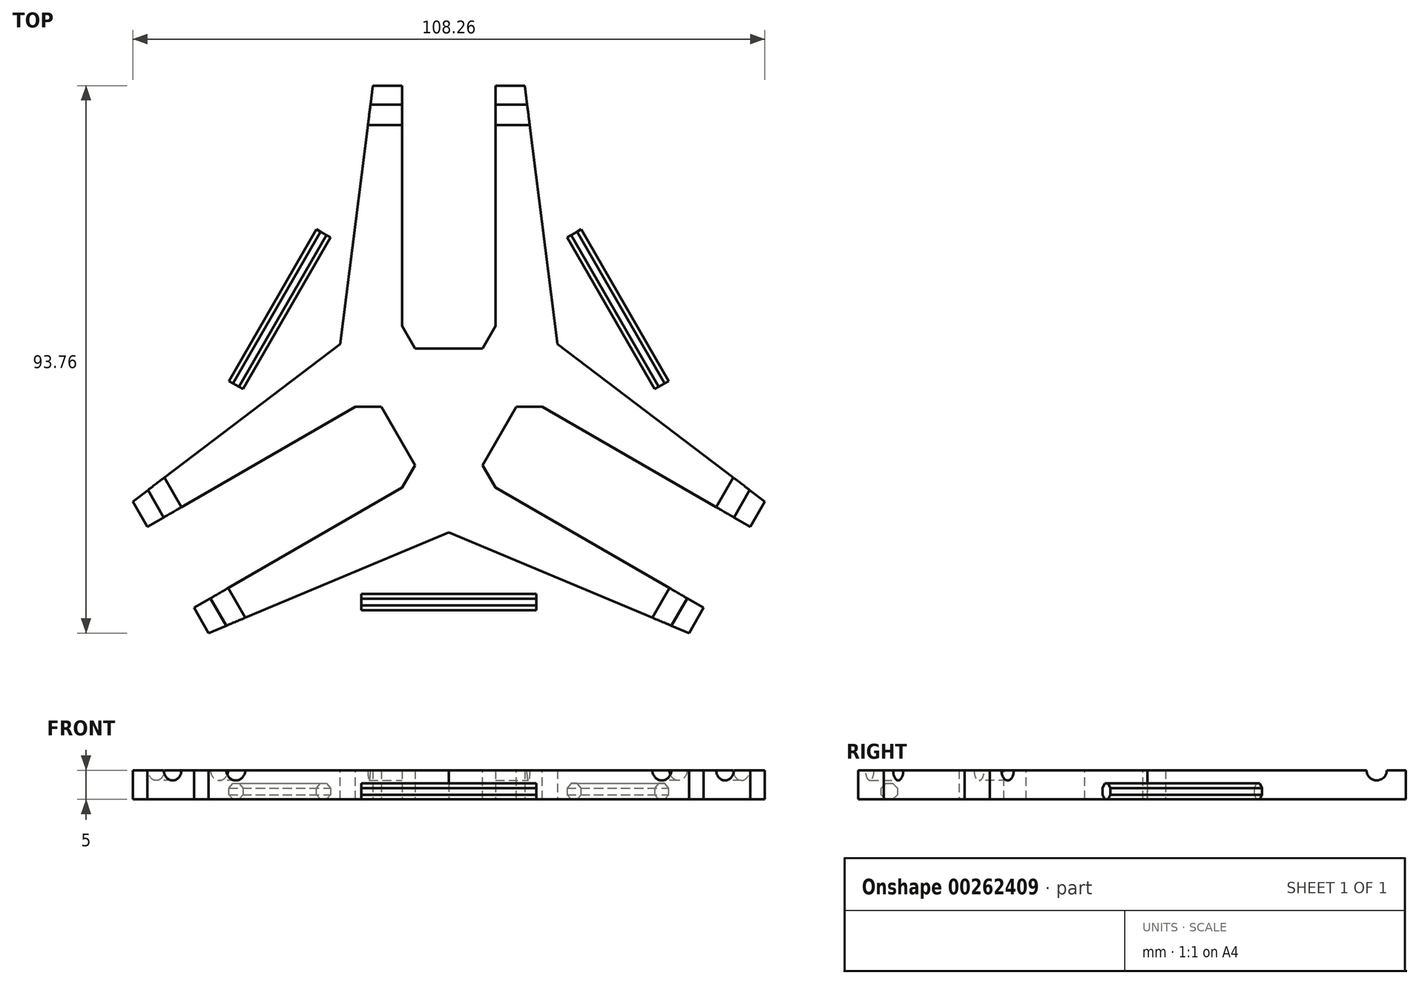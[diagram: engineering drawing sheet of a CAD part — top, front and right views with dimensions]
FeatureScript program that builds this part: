
annotation { "Feature Type Name" : "Feature", "Feature Type Description" : "" }
export const myFeature = defineFeature(function(context is Context, id is Id, definition is map)
    precondition{}
    {
        {
            var Q0;
            Q0=qCreatedBy(makeId("Top.planeOp"),FACE);
            var sketch = newSketch(context, id + "F0", { "sketchPlane" : qUnion([Q0])});
            skLineSegment(sketch, "E0", {"start": v(0, 0) * mm, "end": v(0, 10) * mm});
            skLineSegment(sketch, "E1", {"start": v(0, 10) * mm, "end": v(-8, 10) * mm});
            skLineSegment(sketch, "E2", {"start": v(-8, 10) * mm, "end": v(-8, 55) * mm});
            skLineSegment(sketch, "E3", {"start": v(-8, 55) * mm, "end": v(-13, 55) * mm});
            skLineSegment(sketch, "E4", {"start": v(-13, 55) * mm, "end": v(-20, 0) * mm});
            skLineSegment(sketch, "E5", {"start": v(-20, 0) * mm, "end": v(0, 0) * mm});
            skLineSegment(sketch, "E6.MirrorCS", {"start": v(0, 10) * mm, "end": v(8, 10) * mm});
            skLineSegment(sketch, "E7.MirrorCS", {"start": v(8, 10) * mm, "end": v(8, 55) * mm});
            skLineSegment(sketch, "E8.MirrorCS", {"start": v(8, 55) * mm, "end": v(13, 55) * mm});
            skLineSegment(sketch, "E9.MirrorCS", {"start": v(13, 55) * mm, "end": v(20, 0) * mm});
            skLineSegment(sketch, "E10.MirrorCS", {"start": v(20, 0) * mm, "end": v(0, 0) * mm});
            skSolve(sketch);
        }
        {
            var Q0;
            Q0=makeQuery(id+"F0.imprint","IMPRINT",FACE,{"disambiguationData":[TD([[makeQuery(id+"F0.imprint","IMPRINT",EDGE,{"derivedFrom":sQuery(id+"F0.wireOp",EDGE,"E0")}),-1.0]])]});
            var Q1;
            Q1=makeQuery(id+"F0.imprint","IMPRINT",FACE,{"disambiguationData":[TD([[makeQuery(id+"F0.imprint","IMPRINT",EDGE,{"derivedFrom":sQuery(id+"F0.wireOp",EDGE,"E0")}),1.0]])]});
            extrude(context, id + "F1", {"entities" : qUnion([Q0, Q1]), "depth" : 5 * mm});
        }
        {
            var Q0;
            Q0=qCreatedBy(makeId("Right.planeOp"),FACE);
            var sketch = newSketch(context, id + "F2", { "sketchPlane" : qUnion([Q0])});
            skLineSegment(sketch, "E11.0.0", {"start": v(0, 0) * mm, "end": v(55, 0) * mm, "construction": true});
            skLineSegment(sketch, "E11.0.1", {"start": v(55, 0) * mm, "end": v(55, 5) * mm, "construction": true});
            skLineSegment(sketch, "E11.0.2", {"start": v(55, 5) * mm, "end": v(0, 5) * mm, "construction": true});
            skLineSegment(sketch, "E11.0.3", {"start": v(0, 5) * mm, "end": v(0, 0) * mm, "construction": true});
            skCircle(sketch, "E12", {"center": v(50, 5) * mm, "radius": 1.75 * mm});
            skLineSegment(sketch, "E13", {"start": v(0, 24.2) * mm, "end": v(0, -16.8) * mm, "construction": true});
            skCircle(sketch, "E14.cCircle", {"center": v(-71.43, 1.39) * mm, "radius": 1.5 * mm, "construction": true});
            skLineSegment(sketch, "E14.0", {"start": v(-72, 0) * mm, "end": v(-72.82, 0.81) * mm});
            skLineSegment(sketch, "E14.1", {"start": v(-72.82, 0.81) * mm, "end": v(-72.82, 1.96) * mm});
            skLineSegment(sketch, "E14.2", {"start": v(-72.82, 1.96) * mm, "end": v(-72, 2.77) * mm});
            skLineSegment(sketch, "E14.3", {"start": v(-72, 2.77) * mm, "end": v(-70.86, 2.77) * mm});
            skLineSegment(sketch, "E14.4", {"start": v(-70.86, 2.77) * mm, "end": v(-70.05, 1.96) * mm});
            skLineSegment(sketch, "E14.5", {"start": v(-70.05, 1.96) * mm, "end": v(-70.05, 0.81) * mm});
            skLineSegment(sketch, "E14.6", {"start": v(-70.05, 0.81) * mm, "end": v(-70.86, 0) * mm});
            skLineSegment(sketch, "E14.7", {"start": v(-70.86, 0) * mm, "end": v(-72, 0) * mm});
            skSolve(sketch);
        }
        {
            var Q0;
            Q0=makeQuery(id+"F2.imprint","IMPRINT",FACE,{"disambiguationData":[TD([[makeQuery(id+"F2.imprint","IMPRINT",EDGE,{"derivedFrom":sQuery(id+"F2.wireOp",EDGE,"E12")}),1.0]])]});
            extrude(context, id + "F3", {"entities" : qUnion([Q0]), "operationType" : NewBodyOperationType.REMOVE, "endBound" : BoundingType.SYMMETRIC, "oppositeDirection" : true, "depth" : 50 * mm});
        }
        {
            var Q0;
            Q0=makeQuery(id+"F1.opExtrude","SWEPT_BODY",BODY,{"disambiguationData":[OSD([sQuery(id+"F0.wireOp",EDGE,"E1"),sQuery(id+"F0.wireOp",EDGE,"E2"),sQuery(id+"F0.wireOp",EDGE,"E3"),sQuery(id+"F0.wireOp",EDGE,"E4"),sQuery(id+"F0.wireOp",EDGE,"E5"),sQuery(id+"F0.wireOp",EDGE,"E6.MirrorCS"),sQuery(id+"F0.wireOp",EDGE,"E7.MirrorCS"),sQuery(id+"F0.wireOp",EDGE,"E8.MirrorCS"),sQuery(id+"F0.wireOp",EDGE,"E9.MirrorCS"),sQuery(id+"F0.wireOp",EDGE,"E10.MirrorCS")])]});
            var Q1;
            Q1=sQuery(id+"F2.wireOp",EDGE,"E13");
            circularPattern(context, id + "F4", {"operationType" : NewBodyOperationType.ADD, "entities" : qUnion([Q0]), "axis" : qUnion([Q1]), "angle" : 360 * degree, "instanceCount" : 3, "equalSpace" : true});
        }
        {
            var Q0;
            Q0=makeQuery(id+"F2.imprint","IMPRINT",FACE,{"disambiguationData":[TD([[makeQuery(id+"F2.imprint","IMPRINT",EDGE,{"derivedFrom":sQuery(id+"F2.wireOp",EDGE,"E14.0")}),-1.0]])]});
            extrude(context, id + "F5", {"entities" : qUnion([Q0]), "endBound" : BoundingType.SYMMETRIC, "depth" : 30 * mm});
        }
        {
            var Q0;
            Q0=makeQuery(id+"F5.opExtrude","SWEPT_BODY",BODY,{"disambiguationData":[OSD([sQuery(id+"F2.wireOp",EDGE,"E14.0"),sQuery(id+"F2.wireOp",EDGE,"E14.1"),sQuery(id+"F2.wireOp",EDGE,"E14.2"),sQuery(id+"F2.wireOp",EDGE,"E14.3"),sQuery(id+"F2.wireOp",EDGE,"E14.4"),sQuery(id+"F2.wireOp",EDGE,"E14.5"),sQuery(id+"F2.wireOp",EDGE,"E14.6"),sQuery(id+"F2.wireOp",EDGE,"E14.7")])]});
            transform(context, id + "F6", {"entities" : qUnion([Q0]), "transformType" : TransformType.TRANSLATION_3D, "dx" : 0 * mm, "dy" : 38 * mm, "dz" : 0 * mm, "makeCopy" : false});
        }
        {
            var Q0;
            Q0=makeQuery(id+"F5.opExtrude","SWEPT_BODY",BODY,{"disambiguationData":[OSD([sQuery(id+"F2.wireOp",EDGE,"E14.0"),sQuery(id+"F2.wireOp",EDGE,"E14.1"),sQuery(id+"F2.wireOp",EDGE,"E14.2"),sQuery(id+"F2.wireOp",EDGE,"E14.3"),sQuery(id+"F2.wireOp",EDGE,"E14.4"),sQuery(id+"F2.wireOp",EDGE,"E14.5"),sQuery(id+"F2.wireOp",EDGE,"E14.6"),sQuery(id+"F2.wireOp",EDGE,"E14.7")])]});
            var Q1;
            Q1=sQuery(id+"F2.wireOp",EDGE,"E13");
            circularPattern(context, id + "F7", {"entities" : qUnion([Q0]), "axis" : qUnion([Q1]), "angle" : 360 * degree, "instanceCount" : 3, "equalSpace" : true});
        }
    });
